# Revit family: ARKA-A1415xWSxMPO0500x
name_source: partatom
category: Leuchten
units: mm (PartAtom-declared; Revit-internal decimal feet)

## family parameters
Basisbauteil = Fläche
Beim Laden mit Abzugskörper schneiden = Nein
Bemaßung runder Anschluss = Durchmesser verwenden
Gemeinsam genutzt = Nein
Lichtquelle = Ja
OmniClass-Nummer = 23.80.70.11
OmniClass-Titel = Luminaries for Internal Lighting
Raumberechnungspunkt = Nein
Teiletyp = Normal

## types (8) — shared parameters
Baugruppenkennzeichen = D5020200
Datei für fotometrisches Netz = ARKA-A_MPO.IES
Emissionsform beim Rendern sichtbar = Nein
Farbfilter = 16777215
Farbtemperaturverschiebung bei Dämpfen der Lampe = <Keine Auswahl>
Hersteller = RIDI Leuchten GmbH
Lampe = LED
Neigungswinkel = 90.00°
URL = www.ridi.de
Von Breite des Rechtecks ausssenden = 1407 mm  [stored 4.61614 ft]
Von Länge des Rechtecks aussenden = 164 mm  [stored 0.538058 ft]
brand = RIDI
conformity mark = CE
electrical safety class = 1
height = 48 mm  [stored 0.15748 ft]
ingress protection (IP) code = IP20
length = 1411 mm  [stored 4.62927 ft]
nominal frequency = 50-60Hz
nominal voltage = 230
voltage type (AC, DC, UC) = AC
weight = 5 kg
width = 167 mm  [stored 0.5479 ft]
zero-valued in all types: Vorgabe-Ansicht

## per-type parameters (varying)
| type | Modell | Scheinlast | rated input power |
| ARKA-A1415DAWS830MPO0500 | 0637929 | 37 VA | 37 |
| ARKA-A1415DAWS830MPO0500-SEN | 0637930 | 37 VA | 37 |
| ARKA-A1415DAWS840MPO0500 | 0637931 | 37 VA | 37 |
| ARKA-A1415DAWS840MPO0500-SEN | 0637932 | 37 VA | 37 |
| ARKA-A1415FLWS830MPO0500 | 0627929 | 37 VA | 37 |
| ARKA-A1415FLWS840MPO0500 | 0627931 | 37 VA | 37 |
| ARKA-A1415DAWS8TWMPO0500 | 0637933 | 37 VA | 37 |
| ARKA-A1415DAWS8TWMPO0500-SEN | 0637934 | 38 VA | 38 |

note: column(s) folded — value = type name in every type: product name

note: [stored X ft] marks values corroborated as IEEE doubles in the binary element streams (Revit-internal decimal feet)
